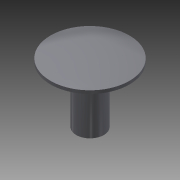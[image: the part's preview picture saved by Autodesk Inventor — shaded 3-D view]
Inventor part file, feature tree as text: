
AUTODESK INVENTOR PART (.ipt)
format: ipt  version: 2011 (Build 150239000, 239)  size: 76,288 bytes
history: native  units: mm (DEFAULTED — no unit token found)
features: sketch x2, reference x2, revolve x1, extrude x1
ambient origin geometry x8: Origin, YZ Plane, XZ Plane, XY Plane, X Axis, Y Axis, Z Axis, Center Point
bodies: Solid1 (feature_tree)
feature tree (6):
  revolve  "Revolution1"  [1 undecoded]
  extrude  "Extrusion1"  [1 undecoded]
  sketch  "Sketch1"  dims[d0=90.0deg d1=3.175mm d2=0.0mm]
  reference  "Reference1"
  reference  "Reference2"
  sketch  "Sketch2"
note: 2 required parameter values undecoded (feature->parameter linkage not recoverable at this tier; creation-order binding heuristic only, values carry confidence <= 0.55)